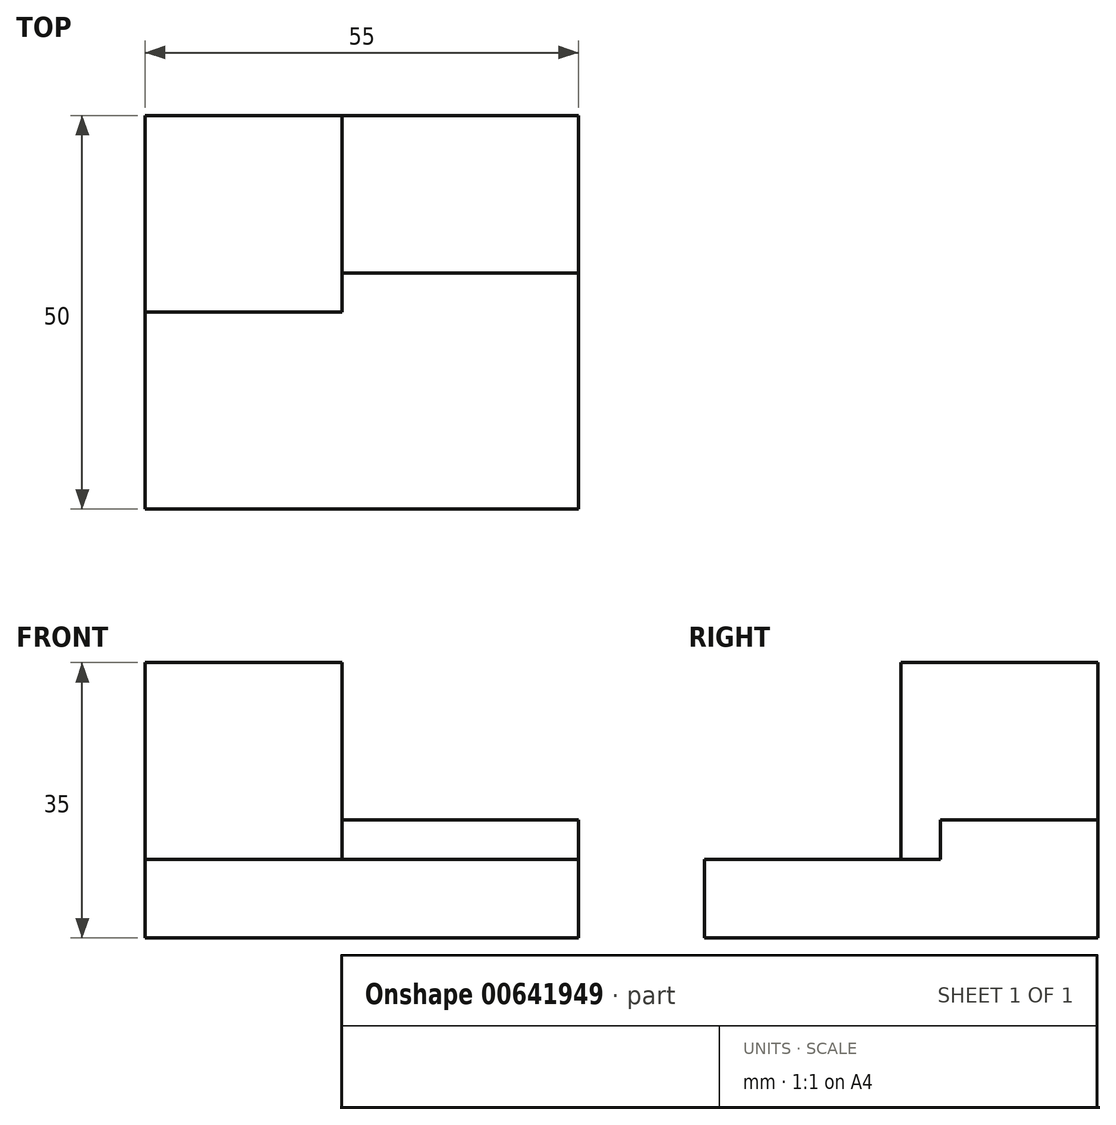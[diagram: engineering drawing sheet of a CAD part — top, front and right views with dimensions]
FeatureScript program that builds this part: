
annotation { "Feature Type Name" : "Feature", "Feature Type Description" : "" }
export const myFeature = defineFeature(function(context is Context, id is Id, definition is map)
    precondition{}
    {
        {
            var Q0;
            Q0=qCreatedBy(makeId("Top.planeOp"),FACE);
            var sketch = newSketch(context, id + "F0", { "sketchPlane" : qUnion([Q0])});
            skLineSegment(sketch, "E0.bottom", {"start": v(27.5, 25) * mm, "end": v(-27.5, 25) * mm});
            skLineSegment(sketch, "E0.top", {"start": v(27.5, -25) * mm, "end": v(-27.5, -25) * mm});
            skLineSegment(sketch, "E0.left", {"start": v(27.5, 25) * mm, "end": v(27.5, -25) * mm});
            skLineSegment(sketch, "E0.right", {"start": v(-27.5, 25) * mm, "end": v(-27.5, -25) * mm});
            skPoint(sketch, "E0.middle", {"position": v(0, 0) * mm});
            skSolve(sketch);
        }
        {
            var Q0;
            Q0 = qSketchRegion(id + "F0", true);
            extrude(context, id + "F1", {"entities" : qUnion([Q0]), "depth" : 10 * mm, "offsetDistance" : 25 * mm});
        }
        {
            var Q0;
            Q0=makeQuery(id+"F1.opExtrude","CAP_FACE",FACE,{"disambiguationData":[OSD([sQuery(id+"F0.wireOp",EDGE,"E0.bottom"),sQuery(id+"F0.wireOp",EDGE,"E0.top"),sQuery(id+"F0.wireOp",EDGE,"E0.left"),sQuery(id+"F0.wireOp",EDGE,"E0.right")])],"isStart":false});
            var sketch = newSketch(context, id + "F2", { "sketchPlane" : qUnion([Q0])});
            skLineSegment(sketch, "E1.bottom", {"start": v(-27.5, 25) * mm, "end": v(-2.5, 25) * mm});
            skLineSegment(sketch, "E1.top", {"start": v(-27.5, 0) * mm, "end": v(-2.5, 0) * mm});
            skLineSegment(sketch, "E1.left", {"start": v(-27.5, 25) * mm, "end": v(-27.5, 0) * mm});
            skLineSegment(sketch, "E1.right", {"start": v(-2.5, 25) * mm, "end": v(-2.5, 0) * mm});
            skSolve(sketch);
        }
        {
            var Q0;
            Q0 = qSketchRegion(id + "F2", true);
            extrude(context, id + "F3", {"entities" : qUnion([Q0]), "operationType" : NewBodyOperationType.ADD, "depth" : 25 * mm, "offsetDistance" : 25 * mm});
        }
        {
            var Q0;
            Q0=makeQuery(id+"F3.opExtrude","SWEPT_FACE",FACE,{"disambiguationData":[OSD([sQuery(id+"F2.wireOp",EDGE,"E1.right")])]});
            var sketch = newSketch(context, id + "F4", { "sketchPlane" : qUnion([Q0])});
            skLineSegment(sketch, "E2.bottom", {"start": v(25, 10) * mm, "end": v(5, 10) * mm});
            skLineSegment(sketch, "E2.top", {"start": v(25, 15) * mm, "end": v(5, 15) * mm});
            skLineSegment(sketch, "E2.left", {"start": v(25, 10) * mm, "end": v(25, 15) * mm});
            skLineSegment(sketch, "E2.right", {"start": v(5, 10) * mm, "end": v(5, 15) * mm});
            skSolve(sketch);
        }
        {
            var Q0;
            Q0 = qSketchRegion(id + "F4", true);
            var Q1;
            Q1=makeQuery(id+"F1.opExtrude","SWEPT_FACE",FACE,{"disambiguationData":[OSD([sQuery(id+"F0.wireOp",EDGE,"E0.left")])]});
            extrude(context, id + "F5", {"entities" : qUnion([Q0]), "operationType" : NewBodyOperationType.ADD, "endBound" : BoundingType.UP_TO_SURFACE, "depth" : 67.1 * mm, "endBoundEntityFace" : qUnion([Q1]), "offsetDistance" : 25 * mm});
        }
    });
